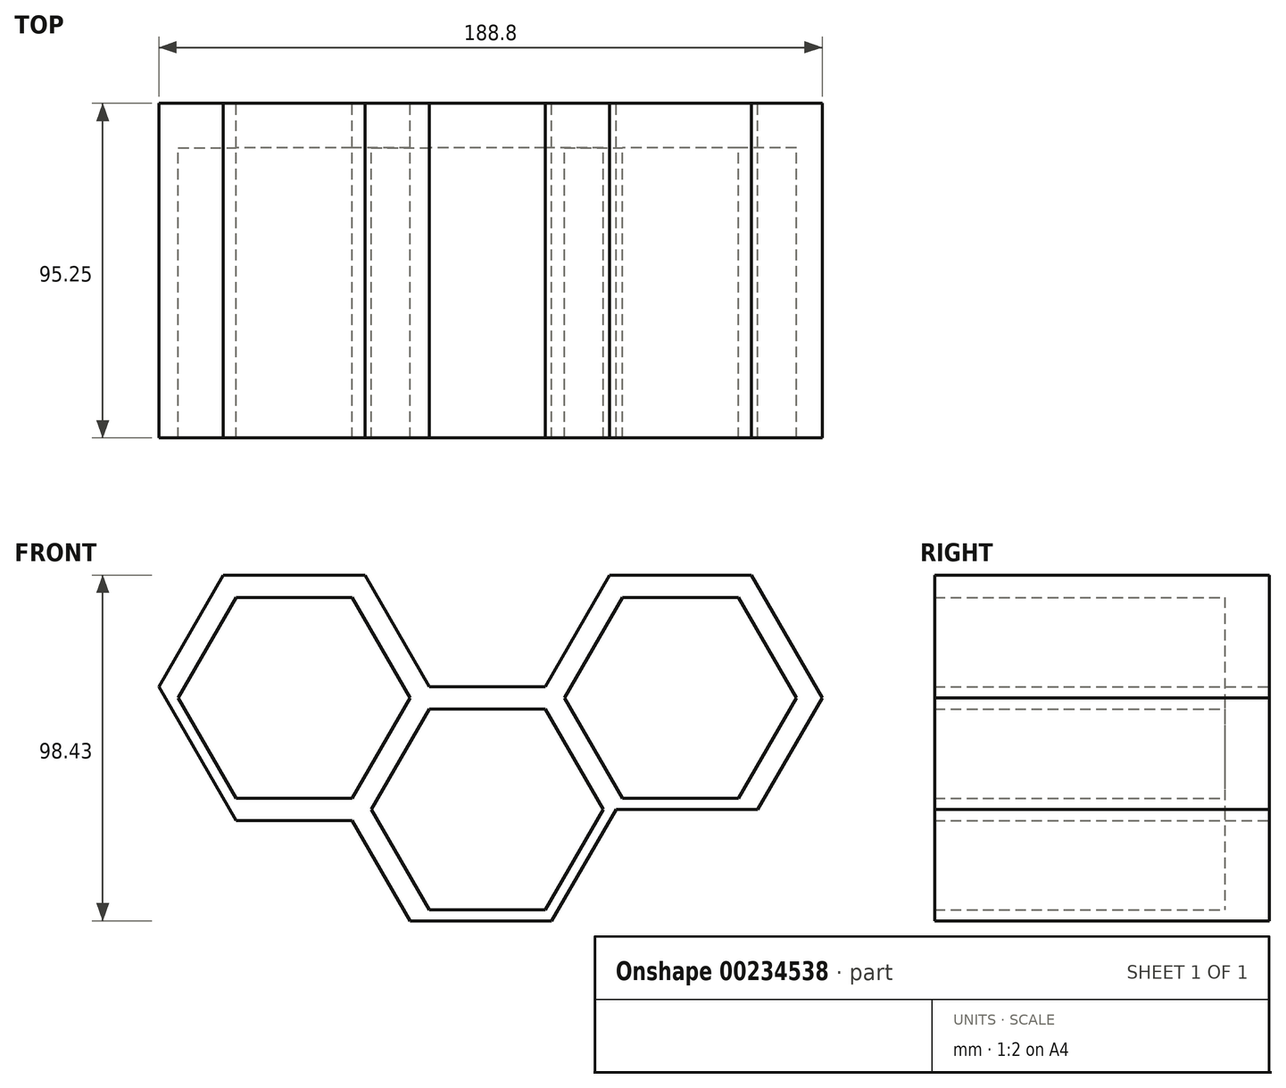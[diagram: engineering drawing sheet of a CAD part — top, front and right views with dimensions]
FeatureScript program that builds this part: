
annotation { "Feature Type Name" : "Feature", "Feature Type Description" : "" }
export const myFeature = defineFeature(function(context is Context, id is Id, definition is map)
    precondition{}
    {
        {
            var Q0;
            Q0=qCreatedBy(makeId("Front.planeOp"),FACE);
            var sketch = newSketch(context, id + "F0", { "sketchPlane" : qUnion([Q0])});
            skLineSegment(sketch, "E0.1", {"start": v(-4.28, 98.54) * mm, "end": v(32.38, 98.54) * mm});
            skLineSegment(sketch, "E1.1", {"start": v(-59.27, 130.3) * mm, "end": v(-27.5, 130.3) * mm});
            skLineSegment(sketch, "E2.2", {"start": v(-77.6, 162.04) * mm, "end": v(-59.27, 130.3) * mm});
            skCircle(sketch, "E3.cCircle", {"center": v(-40.94, 162.04) * mm, "radius": 28.58 * mm, "construction": true});
            skLineSegment(sketch, "E3.0", {"start": v(-73.94, 162.04) * mm, "end": v(-57.44, 190.62) * mm});
            skLineSegment(sketch, "E3.1", {"start": v(-57.44, 190.62) * mm, "end": v(-24.44, 190.62) * mm});
            skLineSegment(sketch, "E3.2", {"start": v(-24.44, 190.62) * mm, "end": v(-7.94, 162.04) * mm});
            skLineSegment(sketch, "E3.3", {"start": v(-7.94, 162.04) * mm, "end": v(-24.44, 133.47) * mm});
            skLineSegment(sketch, "E3.4", {"start": v(-24.44, 133.47) * mm, "end": v(-57.44, 133.47) * mm});
            skLineSegment(sketch, "E3.5", {"start": v(-57.44, 133.47) * mm, "end": v(-73.94, 162.04) * mm});
            skCircle(sketch, "E4.cCircle", {"center": v(-40.94, 162.04) * mm, "radius": 31.75 * mm, "construction": true});
            skLineSegment(sketch, "E4.0", {"start": v(-77.6, 162.04) * mm, "end": v(-59.27, 193.8) * mm});
            skLineSegment(sketch, "E4.1", {"start": v(-59.27, 193.8) * mm, "end": v(-22.6, 193.8) * mm});
            skLineSegment(sketch, "E4.2", {"start": v(-22.6, 193.8) * mm, "end": v(-4.28, 162.04) * mm});
            skLineSegment(sketch, "E4.3", {"start": v(-4.28, 162.04) * mm, "end": v(-22.6, 130.3) * mm});
            skLineSegment(sketch, "E4.4", {"start": v(-22.6, 130.3) * mm, "end": v(-59.27, 130.3) * mm});
            skLineSegment(sketch, "E4.5", {"start": v(-59.27, 130.3) * mm, "end": v(-77.6, 162.04) * mm});
            skPoint(sketch, "E4.0.midPoint", {"position": v(-68.44, 177.92) * mm});
            skCircle(sketch, "E5.cCircle", {"center": v(14.05, 130.3) * mm, "radius": 28.57 * mm, "construction": true});
            skLineSegment(sketch, "E5.0", {"start": v(-18.94, 130.3) * mm, "end": v(-2.45, 158.87) * mm});
            skLineSegment(sketch, "E5.1", {"start": v(-2.45, 158.87) * mm, "end": v(30.55, 158.87) * mm});
            skLineSegment(sketch, "E5.2", {"start": v(30.55, 158.87) * mm, "end": v(47.05, 130.3) * mm});
            skLineSegment(sketch, "E5.3", {"start": v(47.05, 130.3) * mm, "end": v(30.55, 101.72) * mm});
            skLineSegment(sketch, "E5.4", {"start": v(30.55, 101.72) * mm, "end": v(-2.45, 101.72) * mm});
            skLineSegment(sketch, "E5.5", {"start": v(-2.45, 101.72) * mm, "end": v(-18.94, 130.3) * mm});
            skPoint(sketch, "E5.0.midPoint", {"position": v(-10.7, 144.58) * mm});
            skCircle(sketch, "E6.cCircle", {"center": v(14.05, 130.3) * mm, "radius": 31.75 * mm, "construction": true});
            skLineSegment(sketch, "E6.0", {"start": v(-22.6, 130.3) * mm, "end": v(-4.28, 162.04) * mm});
            skLineSegment(sketch, "E6.1", {"start": v(-4.28, 162.04) * mm, "end": v(32.38, 162.04) * mm});
            skLineSegment(sketch, "E6.2", {"start": v(32.38, 162.04) * mm, "end": v(50.71, 130.3) * mm});
            skLineSegment(sketch, "E6.3", {"start": v(50.71, 130.3) * mm, "end": v(32.38, 98.54) * mm});
            skLineSegment(sketch, "E6.4", {"start": v(32.38, 98.54) * mm, "end": v(-4.28, 98.54) * mm});
            skLineSegment(sketch, "E6.5", {"start": v(-4.28, 98.54) * mm, "end": v(-22.6, 130.3) * mm});
            skPoint(sketch, "E6.0.midPoint", {"position": v(-13.44, 146.17) * mm});
            skCircle(sketch, "E7.cCircle", {"center": v(69.05, 162.04) * mm, "radius": 28.58 * mm, "construction": true});
            skLineSegment(sketch, "E7.0", {"start": v(36.05, 162.04) * mm, "end": v(52.55, 190.62) * mm});
            skLineSegment(sketch, "E7.1", {"start": v(52.55, 190.62) * mm, "end": v(85.54, 190.62) * mm});
            skLineSegment(sketch, "E7.2", {"start": v(85.54, 190.62) * mm, "end": v(102.04, 162.04) * mm});
            skLineSegment(sketch, "E7.3", {"start": v(102.04, 162.04) * mm, "end": v(85.54, 133.47) * mm});
            skLineSegment(sketch, "E7.4", {"start": v(85.54, 133.47) * mm, "end": v(52.55, 133.47) * mm});
            skLineSegment(sketch, "E7.5", {"start": v(52.55, 133.47) * mm, "end": v(36.05, 162.04) * mm});
            skPoint(sketch, "E7.0.midPoint", {"position": v(44.3, 176.33) * mm});
            skCircle(sketch, "E8.cCircle", {"center": v(69.05, 162.04) * mm, "radius": 31.75 * mm, "construction": true});
            skLineSegment(sketch, "E8.0", {"start": v(32.38, 162.04) * mm, "end": v(50.71, 193.8) * mm});
            skLineSegment(sketch, "E8.1", {"start": v(50.71, 193.8) * mm, "end": v(87.38, 193.8) * mm});
            skLineSegment(sketch, "E8.2", {"start": v(87.38, 193.8) * mm, "end": v(105.7, 162.04) * mm});
            skLineSegment(sketch, "E8.3", {"start": v(105.7, 162.04) * mm, "end": v(87.38, 130.3) * mm});
            skLineSegment(sketch, "E8.4", {"start": v(87.38, 130.3) * mm, "end": v(50.71, 130.3) * mm});
            skLineSegment(sketch, "E8.5", {"start": v(50.71, 130.3) * mm, "end": v(32.38, 162.04) * mm});
            skPoint(sketch, "E8.0.midPoint", {"position": v(41.55, 177.92) * mm});
            skLineSegment(sketch, "E9.0", {"start": v(32.38, 98.54) * mm, "end": v(50.71, 130.3) * mm});
            skLineSegment(sketch, "E9.1", {"start": v(50.71, 130.3) * mm, "end": v(87.38, 130.3) * mm});
            skPoint(sketch, "E9.0.midPoint", {"position": v(41.55, 114.42) * mm});
            skLineSegment(sketch, "E10", {"start": v(48.88, 196.97) * mm, "end": v(89.2, 196.97) * mm});
            skLineSegment(sketch, "E11", {"start": v(48.88, 196.97) * mm, "end": v(30.55, 165.22) * mm});
            skLineSegment(sketch, "E12", {"start": v(30.55, 165.22) * mm, "end": v(-2.45, 165.22) * mm});
            skLineSegment(sketch, "E13", {"start": v(-2.45, 165.22) * mm, "end": v(-20.78, 196.97) * mm});
            skLineSegment(sketch, "E14", {"start": v(-20.78, 196.97) * mm, "end": v(-61.1, 196.97) * mm});
            skLineSegment(sketch, "E15", {"start": v(-61.1, 196.97) * mm, "end": v(-79.43, 165.22) * mm});
            skLineSegment(sketch, "E16", {"start": v(91.04, 130.3) * mm, "end": v(109.37, 162.04) * mm});
            skLineSegment(sketch, "E17", {"start": v(89.2, 196.97) * mm, "end": v(109.37, 162.04) * mm});
            skLineSegment(sketch, "E18", {"start": v(-7.94, 98.54) * mm, "end": v(-24.44, 127.12) * mm});
            skLineSegment(sketch, "E19", {"start": v(-24.44, 127.12) * mm, "end": v(-57.44, 127.12) * mm});
            skLineSegment(sketch, "E20", {"start": v(-59.27, 130.3) * mm, "end": v(-57.44, 127.12) * mm});
            skLineSegment(sketch, "E21", {"start": v(-4.28, 98.54) * mm, "end": v(-7.94, 98.54) * mm});
            skLineSegment(sketch, "E22", {"start": v(91.04, 130.3) * mm, "end": v(87.38, 130.3) * mm});
            skLineSegment(sketch, "E23", {"start": v(-79.43, 165.22) * mm, "end": v(-77.6, 162.04) * mm});
            skSolve(sketch);
        }
        {
            var Q0;
            Q0=makeQuery(id+"F0.imprint","IMPRINT",FACE,{"disambiguationData":[TD([[makeQuery(id+"F0.imprint","IMPRINT",EDGE,{"derivedFrom":sQuery(id+"F0.wireOp",EDGE,"E3.0")}),-1.0]])]});
            var Q1;
            Q1=makeQuery(id+"F0.imprint","IMPRINT",FACE,{"disambiguationData":[TD([[makeQuery(id+"F0.imprint","IMPRINT",EDGE,{"derivedFrom":sQuery(id+"F0.wireOp",EDGE,"ae29455d-c252-400a-b569-c5a1c48e1351.0")}),-1.0]])]});
            var Q2;
            Q2=makeQuery(id+"F0.imprint","IMPRINT",FACE,{"disambiguationData":[TD([[makeQuery(id+"F0.imprint","IMPRINT",EDGE,{"derivedFrom":sQuery(id+"F0.wireOp",EDGE,"E7.0")}),-1.0]])]});
            var Q3;
            Q3=makeQuery(id+"F0.imprint","IMPRINT",FACE,{"disambiguationData":[TD([[makeQuery(id+"F0.imprint","IMPRINT",EDGE,{"derivedFrom":sQuery(id+"F0.wireOp",EDGE,"b43d4d8c-f78a-4ff8-8565-99a66ce6ec5f.0")}),-1.0]])]});
            var Q4;
            Q4=makeQuery(id+"F0.imprint","IMPRINT",FACE,{"disambiguationData":[TD([[makeQuery(id+"F0.imprint","IMPRINT",EDGE,{"derivedFrom":sQuery(id+"F0.wireOp",EDGE,"8c75d941-d110-4871-aa41-90a72d60fb2b.0")}),-1.0]])]});
            var Q5;
            Q5=makeQuery(id+"F0.imprint","IMPRINT",FACE,{"disambiguationData":[TD([[makeQuery(id+"F0.imprint","IMPRINT",EDGE,{"derivedFrom":sQuery(id+"F0.wireOp",EDGE,"258573fa-3544-418e-8bc5-5d37e5b8ba09.0")}),-1.0]])]});
            var Q6;
            Q6=makeQuery(id+"F0.imprint","IMPRINT",FACE,{"disambiguationData":[TD([[makeQuery(id+"F0.imprint","IMPRINT",EDGE,{"derivedFrom":sQuery(id+"F0.wireOp",EDGE,"0bf0733b-7d93-4c2e-8366-56d2cde24658.0")}),-1.0]])]});
            var Q7;
            Q7=makeQuery(id+"F0.imprint","IMPRINT",FACE,{"disambiguationData":[TD([[makeQuery(id+"F0.imprint","IMPRINT",EDGE,{"derivedFrom":sQuery(id+"F0.wireOp",EDGE,"93717492-86db-456f-ae55-f71e4e93837b.0")}),-1.0]])]});
            var Q8;
            Q8=makeQuery(id+"F0.imprint","IMPRINT",FACE,{"disambiguationData":[TD([[makeQuery(id+"F0.imprint","IMPRINT",EDGE,{"derivedFrom":sQuery(id+"F0.wireOp",EDGE,"f16ea8c9-6b67-4651-8441-f7eb3c0ce7d7.0")}),-1.0]])]});
            var Q9;
            Q9=makeQuery(id+"F0.imprint","IMPRINT",FACE,{"disambiguationData":[TD([[makeQuery(id+"F0.imprint","IMPRINT",EDGE,{"derivedFrom":sQuery(id+"F0.wireOp",EDGE,"0306a0a6-7289-4661-a415-5fa5585f2cb5.0")}),-1.0]])]});
            var Q10;
            Q10=makeQuery(id+"F0.imprint","IMPRINT",FACE,{"disambiguationData":[TD([[makeQuery(id+"F0.imprint","IMPRINT",EDGE,{"derivedFrom":sQuery(id+"F0.wireOp",EDGE,"0a91a14e-ea0c-483f-91eb-c48bd73cb0e6.0")}),-1.0]])]});
            var Q11;
            Q11=makeQuery(id+"F0.imprint","IMPRINT",FACE,{"disambiguationData":[TD([[makeQuery(id+"F0.imprint","IMPRINT",EDGE,{"derivedFrom":sQuery(id+"F0.wireOp",EDGE,"cbfd9497-f7fe-4f18-9288-d90aa8075d81.0")}),-1.0]])]});
            var Q12;
            Q12=makeQuery(id+"F0.imprint","IMPRINT",FACE,{"disambiguationData":[TD([[makeQuery(id+"F0.imprint","IMPRINT",EDGE,{"derivedFrom":sQuery(id+"F0.wireOp",EDGE,"6282d196-dd8f-4bb0-bca4-b9108e277473.0")}),-1.0]])]});
            var Q13;
            Q13=makeQuery(id+"F0.imprint","IMPRINT",FACE,{"disambiguationData":[TD([[makeQuery(id+"F0.imprint","IMPRINT",EDGE,{"derivedFrom":sQuery(id+"F0.wireOp",EDGE,"084ca30c-4dc0-463f-bfd9-557787ed9a2f.0")}),-1.0]])]});
            var Q14;
            Q14=makeQuery(id+"F0.imprint","IMPRINT",FACE,{"disambiguationData":[TD([[makeQuery(id+"F0.imprint","IMPRINT",EDGE,{"derivedFrom":sQuery(id+"F0.wireOp",EDGE,"06c29831-6b25-410b-9247-4ee044b7735c.0")}),-1.0]])]});
            var Q15;
            Q15=makeQuery(id+"F0.imprint","IMPRINT",FACE,{"disambiguationData":[TD([[makeQuery(id+"F0.imprint","IMPRINT",EDGE,{"derivedFrom":sQuery(id+"F0.wireOp",EDGE,"E5.0")}),-1.0]])]});
            var Q16;
            Q16=makeQuery(id+"F0.imprint","IMPRINT",FACE,{"disambiguationData":[TD([[makeQuery(id+"F0.imprint","IMPRINT",EDGE,{"derivedFrom":sQuery(id+"F0.wireOp",EDGE,"2e929887-9bb9-4083-9cef-f9a6a24e8e46.0")}),-1.0]])]});
            var Q17;
            Q17=makeQuery(id+"F0.imprint","IMPRINT",FACE,{"disambiguationData":[TD([[makeQuery(id+"F0.imprint","IMPRINT",EDGE,{"derivedFrom":sQuery(id+"F0.wireOp",EDGE,"23671680-92ab-419e-a071-eb0943a5012b.0")}),-1.0]])]});
            var Q18;
            Q18=makeQuery(id+"F0.imprint","IMPRINT",FACE,{"disambiguationData":[TD([[makeQuery(id+"F0.imprint","IMPRINT",EDGE,{"derivedFrom":sQuery(id+"F0.wireOp",EDGE,"a1daa6ae-7864-4614-8fb9-3511dddc1266.0")}),-1.0]])]});
            var Q19;
            Q19=makeQuery(id+"F0.imprint","IMPRINT",FACE,{"disambiguationData":[TD([[makeQuery(id+"F0.imprint","IMPRINT",EDGE,{"derivedFrom":sQuery(id+"F0.wireOp",EDGE,"37efd634-c264-4683-8864-08b38c7986ca.0")}),-1.0]])]});
            var Q20;
            Q20=makeQuery(id+"F0.imprint","IMPRINT",FACE,{"disambiguationData":[TD([[makeQuery(id+"F0.imprint","IMPRINT",EDGE,{"derivedFrom":sQuery(id+"F0.wireOp",EDGE,"f2dd3995-374a-43c5-8725-4a87181dc8c5.0")}),-1.0]])]});
            var Q21;
            Q21=makeQuery(id+"F0.imprint","IMPRINT",FACE,{"disambiguationData":[TD([[makeQuery(id+"F0.imprint","IMPRINT",EDGE,{"derivedFrom":sQuery(id+"F0.wireOp",EDGE,"1f2aec04-a318-49b9-a42e-ea2fce35ed6c.0")}),-1.0]])]});
            var Q22;
            Q22=makeQuery(id+"F0.imprint","IMPRINT",FACE,{"disambiguationData":[TD([[makeQuery(id+"F0.imprint","IMPRINT",EDGE,{"derivedFrom":sQuery(id+"F0.wireOp",EDGE,"f97fdbdd-69fc-44f1-b8f7-f6a6a25558e6.0")}),-1.0]])]});
            var Q23;
            Q23=makeQuery(id+"F0.imprint","IMPRINT",FACE,{"disambiguationData":[TD([[makeQuery(id+"F0.imprint","IMPRINT",EDGE,{"derivedFrom":sQuery(id+"F0.wireOp",EDGE,"4e92e904-9607-490d-a429-b319c41500d9.0")}),-1.0]])]});
            var Q24;
            Q24=makeQuery(id+"F0.imprint","IMPRINT",FACE,{"disambiguationData":[TD([[makeQuery(id+"F0.imprint","IMPRINT",EDGE,{"derivedFrom":sQuery(id+"F0.wireOp",EDGE,"084ca30c-4dc0-463f-bfd9-557787ed9a2f.0")}),1.0]])]});
            var Q25;
            Q25=makeQuery(id+"F0.imprint","IMPRINT",FACE,{"disambiguationData":[TD([[makeQuery(id+"F0.imprint","IMPRINT",EDGE,{"derivedFrom":sQuery(id+"F0.wireOp",EDGE,"1f2aec04-a318-49b9-a42e-ea2fce35ed6c.0")}),1.0]])]});
            var Q26;
            Q26=makeQuery(id+"F0.imprint","IMPRINT",FACE,{"disambiguationData":[TD([[makeQuery(id+"F0.imprint","IMPRINT",EDGE,{"derivedFrom":sQuery(id+"F0.wireOp",EDGE,"23671680-92ab-419e-a071-eb0943a5012b.0")}),1.0]])]});
            var Q27;
            Q27=makeQuery(id+"F0.imprint","IMPRINT",FACE,{"disambiguationData":[TD([[makeQuery(id+"F0.imprint","IMPRINT",EDGE,{"derivedFrom":sQuery(id+"F0.wireOp",EDGE,"2e929887-9bb9-4083-9cef-f9a6a24e8e46.0")}),1.0]])]});
            var Q28;
            Q28=makeQuery(id+"F0.imprint","IMPRINT",FACE,{"disambiguationData":[TD([[makeQuery(id+"F0.imprint","IMPRINT",EDGE,{"derivedFrom":sQuery(id+"F0.wireOp",EDGE,"4e92e904-9607-490d-a429-b319c41500d9.0")}),1.0]])]});
            var Q29;
            Q29=makeQuery(id+"F0.imprint","IMPRINT",FACE,{"disambiguationData":[TD([[makeQuery(id+"F0.imprint","IMPRINT",EDGE,{"derivedFrom":sQuery(id+"F0.wireOp",EDGE,"b43d4d8c-f78a-4ff8-8565-99a66ce6ec5f.0")}),1.0]])]});
            var Q30;
            Q30=makeQuery(id+"F0.imprint","IMPRINT",FACE,{"disambiguationData":[TD([[makeQuery(id+"F0.imprint","IMPRINT",EDGE,{"derivedFrom":sQuery(id+"F0.wireOp",EDGE,"ae29455d-c252-400a-b569-c5a1c48e1351.0")}),1.0]])]});
            var Q31;
            Q31=makeQuery(id+"F0.imprint","IMPRINT",FACE,{"disambiguationData":[TD([[makeQuery(id+"F0.imprint","IMPRINT",EDGE,{"derivedFrom":sQuery(id+"F0.wireOp",EDGE,"0a91a14e-ea0c-483f-91eb-c48bd73cb0e6.0")}),1.0]])]});
            var Q32;
            Q32=makeQuery(id+"F0.imprint","IMPRINT",FACE,{"disambiguationData":[TD([[makeQuery(id+"F0.imprint","IMPRINT",EDGE,{"derivedFrom":sQuery(id+"F0.wireOp",EDGE,"258573fa-3544-418e-8bc5-5d37e5b8ba09.0")}),1.0]])]});
            var Q33;
            Q33=makeQuery(id+"F0.imprint","IMPRINT",FACE,{"disambiguationData":[TD([[makeQuery(id+"F0.imprint","IMPRINT",EDGE,{"derivedFrom":sQuery(id+"F0.wireOp",EDGE,"cbfd9497-f7fe-4f18-9288-d90aa8075d81.0")}),1.0]])]});
            var Q34;
            Q34=makeQuery(id+"F0.imprint","IMPRINT",FACE,{"disambiguationData":[TD([[makeQuery(id+"F0.imprint","IMPRINT",EDGE,{"derivedFrom":sQuery(id+"F0.wireOp",EDGE,"f97fdbdd-69fc-44f1-b8f7-f6a6a25558e6.0")}),1.0]])]});
            var Q35;
            Q35=makeQuery(id+"F0.imprint","IMPRINT",FACE,{"disambiguationData":[TD([[makeQuery(id+"F0.imprint","IMPRINT",EDGE,{"derivedFrom":sQuery(id+"F0.wireOp",EDGE,"E5.0")}),1.0]])]});
            var Q36;
            Q36=makeQuery(id+"F0.imprint","IMPRINT",FACE,{"disambiguationData":[TD([[makeQuery(id+"F0.imprint","IMPRINT",EDGE,{"derivedFrom":sQuery(id+"F0.wireOp",EDGE,"8c75d941-d110-4871-aa41-90a72d60fb2b.0")}),1.0]])]});
            var Q37;
            Q37=makeQuery(id+"F0.imprint","IMPRINT",FACE,{"disambiguationData":[TD([[makeQuery(id+"F0.imprint","IMPRINT",EDGE,{"derivedFrom":sQuery(id+"F0.wireOp",EDGE,"f16ea8c9-6b67-4651-8441-f7eb3c0ce7d7.0")}),1.0]])]});
            var Q38;
            Q38=makeQuery(id+"F0.imprint","IMPRINT",FACE,{"disambiguationData":[TD([[makeQuery(id+"F0.imprint","IMPRINT",EDGE,{"derivedFrom":sQuery(id+"F0.wireOp",EDGE,"37efd634-c264-4683-8864-08b38c7986ca.0")}),1.0]])]});
            var Q39;
            Q39=makeQuery(id+"F0.imprint","IMPRINT",FACE,{"disambiguationData":[TD([[makeQuery(id+"F0.imprint","IMPRINT",EDGE,{"derivedFrom":sQuery(id+"F0.wireOp",EDGE,"E3.0")}),1.0]])]});
            var Q40;
            Q40=makeQuery(id+"F0.imprint","IMPRINT",FACE,{"disambiguationData":[TD([[makeQuery(id+"F0.imprint","IMPRINT",EDGE,{"derivedFrom":sQuery(id+"F0.wireOp",EDGE,"0306a0a6-7289-4661-a415-5fa5585f2cb5.0")}),1.0]])]});
            var Q41;
            Q41=makeQuery(id+"F0.imprint","IMPRINT",FACE,{"disambiguationData":[TD([[makeQuery(id+"F0.imprint","IMPRINT",EDGE,{"derivedFrom":sQuery(id+"F0.wireOp",EDGE,"0bf0733b-7d93-4c2e-8366-56d2cde24658.0")}),1.0]])]});
            var Q42;
            Q42=makeQuery(id+"F0.imprint","IMPRINT",FACE,{"disambiguationData":[TD([[makeQuery(id+"F0.imprint","IMPRINT",EDGE,{"derivedFrom":sQuery(id+"F0.wireOp",EDGE,"06c29831-6b25-410b-9247-4ee044b7735c.0")}),1.0]])]});
            var Q43;
            Q43=makeQuery(id+"F0.imprint","IMPRINT",FACE,{"disambiguationData":[TD([[makeQuery(id+"F0.imprint","IMPRINT",EDGE,{"derivedFrom":sQuery(id+"F0.wireOp",EDGE,"6282d196-dd8f-4bb0-bca4-b9108e277473.0")}),1.0]])]});
            var Q44;
            Q44=makeQuery(id+"F0.imprint","IMPRINT",FACE,{"disambiguationData":[TD([[makeQuery(id+"F0.imprint","IMPRINT",EDGE,{"derivedFrom":sQuery(id+"F0.wireOp",EDGE,"E7.0")}),1.0]])]});
            var Q45;
            Q45=makeQuery(id+"F0.imprint","IMPRINT",FACE,{"disambiguationData":[TD([[makeQuery(id+"F0.imprint","IMPRINT",EDGE,{"derivedFrom":sQuery(id+"F0.wireOp",EDGE,"f2dd3995-374a-43c5-8725-4a87181dc8c5.0")}),1.0]])]});
            var Q46;
            Q46=makeQuery(id+"F0.imprint","IMPRINT",FACE,{"disambiguationData":[TD([[makeQuery(id+"F0.imprint","IMPRINT",EDGE,{"derivedFrom":sQuery(id+"F0.wireOp",EDGE,"a1daa6ae-7864-4614-8fb9-3511dddc1266.0")}),1.0]])]});
            var Q47;
            Q47=makeQuery(id+"F0.imprint","IMPRINT",FACE,{"disambiguationData":[TD([[makeQuery(id+"F0.imprint","IMPRINT",EDGE,{"derivedFrom":sQuery(id+"F0.wireOp",EDGE,"93717492-86db-456f-ae55-f71e4e93837b.0")}),1.0]])]});
            extrude(context, id + "F1", {"entities" : qUnion([Q0, Q1, Q2, Q3, Q4, Q5, Q6, Q7, Q8, Q9, Q10, Q11, Q12, Q13, Q14, Q15, Q16, Q17, Q18, Q19, Q20, Q21, Q22, Q23, Q24, Q25, Q26, Q27, Q28, Q29, Q30, Q31, Q32, Q33, Q34, Q35, Q36, Q37, Q38, Q39, Q40, Q41, Q42, Q43, Q44, Q45, Q46, Q47]), "depth" : 12.7 * mm, "offsetDistance" : 25.4 * mm});
        }
        {
            var Q0;
            Q0=makeQuery(id+"F0.imprint","IMPRINT",FACE,{"disambiguationData":[TD([[makeQuery(id+"F0.imprint","IMPRINT",EDGE,{"derivedFrom":sQuery(id+"F0.wireOp",EDGE,"8c75d941-d110-4871-aa41-90a72d60fb2b.0")}),1.0]])]});
            var Q1;
            Q1=makeQuery(id+"F0.imprint","IMPRINT",FACE,{"disambiguationData":[TD([[makeQuery(id+"F0.imprint","IMPRINT",EDGE,{"derivedFrom":sQuery(id+"F0.wireOp",EDGE,"E5.0")}),1.0]])]});
            var Q2;
            Q2=makeQuery(id+"F0.imprint","IMPRINT",FACE,{"disambiguationData":[TD([[makeQuery(id+"F0.imprint","IMPRINT",EDGE,{"derivedFrom":sQuery(id+"F0.wireOp",EDGE,"E7.0")}),1.0]])]});
            var Q3;
            Q3=makeQuery(id+"F0.imprint","IMPRINT",FACE,{"disambiguationData":[TD([[makeQuery(id+"F0.imprint","IMPRINT",EDGE,{"derivedFrom":sQuery(id+"F0.wireOp",EDGE,"E3.0")}),1.0]])]});
            var Q4;
            Q4=makeQuery(id+"F0.imprint","IMPRINT",FACE,{"disambiguationData":[TD([[makeQuery(id+"F0.imprint","IMPRINT",EDGE,{"derivedFrom":sQuery(id+"F0.wireOp",EDGE,"0306a0a6-7289-4661-a415-5fa5585f2cb5.0")}),1.0]])]});
            var Q5;
            Q5=makeQuery(id+"F0.imprint","IMPRINT",FACE,{"disambiguationData":[TD([[makeQuery(id+"F0.imprint","IMPRINT",EDGE,{"derivedFrom":sQuery(id+"F0.wireOp",EDGE,"084ca30c-4dc0-463f-bfd9-557787ed9a2f.0")}),1.0]])]});
            var Q6;
            Q6=makeQuery(id+"F0.imprint","IMPRINT",FACE,{"disambiguationData":[TD([[makeQuery(id+"F0.imprint","IMPRINT",EDGE,{"derivedFrom":sQuery(id+"F0.wireOp",EDGE,"4e92e904-9607-490d-a429-b319c41500d9.0")}),1.0]])]});
            var Q7;
            Q7=makeQuery(id+"F0.imprint","IMPRINT",FACE,{"disambiguationData":[TD([[makeQuery(id+"F0.imprint","IMPRINT",EDGE,{"derivedFrom":sQuery(id+"F0.wireOp",EDGE,"a1daa6ae-7864-4614-8fb9-3511dddc1266.0")}),1.0]])]});
            var Q8;
            Q8=makeQuery(id+"F0.imprint","IMPRINT",FACE,{"disambiguationData":[TD([[makeQuery(id+"F0.imprint","IMPRINT",EDGE,{"derivedFrom":sQuery(id+"F0.wireOp",EDGE,"93717492-86db-456f-ae55-f71e4e93837b.0")}),1.0]])]});
            var Q9;
            Q9=makeQuery(id+"F0.imprint","IMPRINT",FACE,{"disambiguationData":[TD([[makeQuery(id+"F0.imprint","IMPRINT",EDGE,{"derivedFrom":sQuery(id+"F0.wireOp",EDGE,"258573fa-3544-418e-8bc5-5d37e5b8ba09.0")}),1.0]])]});
            var Q10;
            Q10=makeQuery(id+"F0.imprint","IMPRINT",FACE,{"disambiguationData":[TD([[makeQuery(id+"F0.imprint","IMPRINT",EDGE,{"derivedFrom":sQuery(id+"F0.wireOp",EDGE,"f2dd3995-374a-43c5-8725-4a87181dc8c5.0")}),1.0]])]});
            var Q11;
            Q11=makeQuery(id+"F0.imprint","IMPRINT",FACE,{"disambiguationData":[TD([[makeQuery(id+"F0.imprint","IMPRINT",EDGE,{"derivedFrom":sQuery(id+"F0.wireOp",EDGE,"23671680-92ab-419e-a071-eb0943a5012b.0")}),1.0]])]});
            var Q12;
            Q12=makeQuery(id+"F0.imprint","IMPRINT",FACE,{"disambiguationData":[TD([[makeQuery(id+"F0.imprint","IMPRINT",EDGE,{"derivedFrom":sQuery(id+"F0.wireOp",EDGE,"06c29831-6b25-410b-9247-4ee044b7735c.0")}),1.0]])]});
            var Q13;
            Q13=makeQuery(id+"F0.imprint","IMPRINT",FACE,{"disambiguationData":[TD([[makeQuery(id+"F0.imprint","IMPRINT",EDGE,{"derivedFrom":sQuery(id+"F0.wireOp",EDGE,"ae29455d-c252-400a-b569-c5a1c48e1351.0")}),1.0]])]});
            var Q14;
            Q14=makeQuery(id+"F0.imprint","IMPRINT",FACE,{"disambiguationData":[TD([[makeQuery(id+"F0.imprint","IMPRINT",EDGE,{"derivedFrom":sQuery(id+"F0.wireOp",EDGE,"f97fdbdd-69fc-44f1-b8f7-f6a6a25558e6.0")}),1.0]])]});
            var Q15;
            Q15=makeQuery(id+"F0.imprint","IMPRINT",FACE,{"disambiguationData":[TD([[makeQuery(id+"F0.imprint","IMPRINT",EDGE,{"derivedFrom":sQuery(id+"F0.wireOp",EDGE,"2e929887-9bb9-4083-9cef-f9a6a24e8e46.0")}),1.0]])]});
            var Q16;
            Q16=makeQuery(id+"F0.imprint","IMPRINT",FACE,{"disambiguationData":[TD([[makeQuery(id+"F0.imprint","IMPRINT",EDGE,{"derivedFrom":sQuery(id+"F0.wireOp",EDGE,"0a91a14e-ea0c-483f-91eb-c48bd73cb0e6.0")}),1.0]])]});
            var Q17;
            Q17=makeQuery(id+"F0.imprint","IMPRINT",FACE,{"disambiguationData":[TD([[makeQuery(id+"F0.imprint","IMPRINT",EDGE,{"derivedFrom":sQuery(id+"F0.wireOp",EDGE,"37efd634-c264-4683-8864-08b38c7986ca.0")}),1.0]])]});
            var Q18;
            Q18=makeQuery(id+"F0.imprint","IMPRINT",FACE,{"disambiguationData":[TD([[makeQuery(id+"F0.imprint","IMPRINT",EDGE,{"derivedFrom":sQuery(id+"F0.wireOp",EDGE,"cbfd9497-f7fe-4f18-9288-d90aa8075d81.0")}),1.0]])]});
            var Q19;
            Q19=makeQuery(id+"F0.imprint","IMPRINT",FACE,{"disambiguationData":[TD([[makeQuery(id+"F0.imprint","IMPRINT",EDGE,{"derivedFrom":sQuery(id+"F0.wireOp",EDGE,"6282d196-dd8f-4bb0-bca4-b9108e277473.0")}),1.0]])]});
            var Q20;
            Q20=makeQuery(id+"F0.imprint","IMPRINT",FACE,{"disambiguationData":[TD([[makeQuery(id+"F0.imprint","IMPRINT",EDGE,{"derivedFrom":sQuery(id+"F0.wireOp",EDGE,"0bf0733b-7d93-4c2e-8366-56d2cde24658.0")}),1.0]])]});
            var Q21;
            Q21=makeQuery(id+"F0.imprint","IMPRINT",FACE,{"disambiguationData":[TD([[makeQuery(id+"F0.imprint","IMPRINT",EDGE,{"derivedFrom":sQuery(id+"F0.wireOp",EDGE,"b43d4d8c-f78a-4ff8-8565-99a66ce6ec5f.0")}),1.0]])]});
            var Q22;
            Q22=makeQuery(id+"F0.imprint","IMPRINT",FACE,{"disambiguationData":[TD([[makeQuery(id+"F0.imprint","IMPRINT",EDGE,{"derivedFrom":sQuery(id+"F0.wireOp",EDGE,"f16ea8c9-6b67-4651-8441-f7eb3c0ce7d7.0")}),1.0]])]});
            var Q23;
            Q23=makeQuery(id+"F0.imprint","IMPRINT",FACE,{"disambiguationData":[TD([[makeQuery(id+"F0.imprint","IMPRINT",EDGE,{"derivedFrom":sQuery(id+"F0.wireOp",EDGE,"1f2aec04-a318-49b9-a42e-ea2fce35ed6c.0")}),1.0]])]});
            var Q24;
            {var subQ6=sQuery(id+"F0.wireOp",EDGE,"16495d92-3f2e-4778-aa2a-097d1cd616f4.3");Q24=makeQuery(id+"F0.imprint","IMPRINT",FACE,{"disambiguationData":[TD([[makeQuery(id+"F0.imprint","IMPRINT",EDGE,{"derivedFrom":subQ6}),1.0]])]});}
            var Q25;
            Q25=makeQuery(id+"F0.imprint","IMPRINT",FACE,{"disambiguationData":[TD([[makeQuery(id+"F0.imprint","IMPRINT",EDGE,{"derivedFrom":sQuery(id+"F0.wireOp",EDGE,"16495d92-3f2e-4778-aa2a-097d1cd616f4.1")}),1.0]])]});
            var Q26;
            Q26=makeQuery(id+"F0.imprint","IMPRINT",FACE,{"disambiguationData":[TD([[makeQuery(id+"F0.imprint","IMPRINT",EDGE,{"derivedFrom":sQuery(id+"F0.wireOp",EDGE,"E4.0")}),1.0]])]});
            var Q27;
            {var subQ0=sQuery(id+"F0.wireOp",EDGE,"E6.5");Q27=makeQuery(id+"F0.imprint","IMPRINT",FACE,{"disambiguationData":[TD([[makeQuery(id+"F0.imprint","IMPRINT",EDGE,{"derivedFrom":subQ0}),1.0]])]});}
            extrude(context, id + "F2", {"entities" : qUnion([Q0, Q1, Q2, Q3, Q4, Q5, Q6, Q7, Q8, Q9, Q10, Q11, Q12, Q13, Q14, Q15, Q16, Q17, Q18, Q19, Q20, Q21, Q22, Q23, Q24, Q25, Q26, Q27]), "operationType" : NewBodyOperationType.ADD, "depth" : 95.25 * mm, "offsetDistance" : 25.4 * mm});
        }
    });
